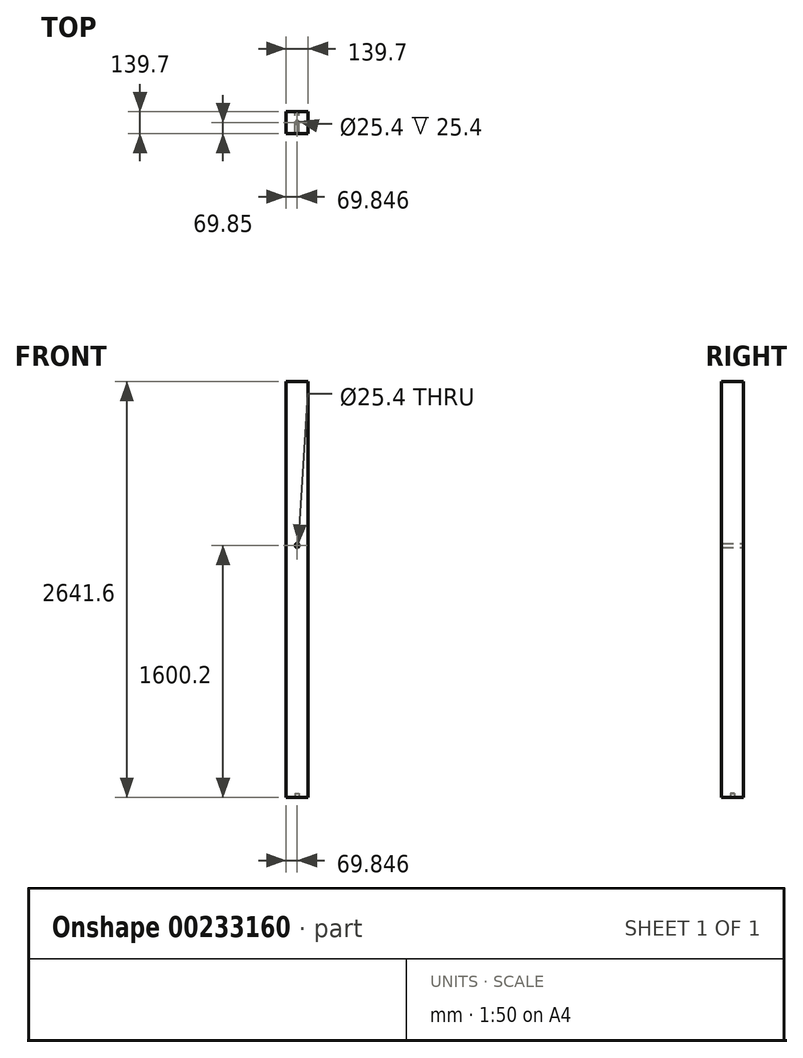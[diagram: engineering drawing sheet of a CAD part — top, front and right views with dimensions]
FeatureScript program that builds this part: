
annotation { "Feature Type Name" : "Feature", "Feature Type Description" : "" }
export const myFeature = defineFeature(function(context is Context, id is Id, definition is map)
    precondition{}
    {
        {
            var Q0;
            Q0=qCreatedBy(makeId("Front.planeOp"),FACE);
            var sketch = newSketch(context, id + "F0", { "sketchPlane" : qUnion([Q0])});
            skLineSegment(sketch, "E0.bottom", {"start": v(-168.05, 2571.7) * mm, "end": v(-28.35, 2571.7) * mm});
            skLineSegment(sketch, "E0.top", {"start": v(-168.05, -69.9) * mm, "end": v(-28.35, -69.9) * mm});
            skLineSegment(sketch, "E0.left", {"start": v(-168.05, 2571.7) * mm, "end": v(-168.05, -69.9) * mm});
            skLineSegment(sketch, "E0.right", {"start": v(-28.35, 2571.7) * mm, "end": v(-28.35, -69.9) * mm});
            skCircle(sketch, "E1", {"center": v(-98.2, 1530.3) * mm, "radius": 12.7 * mm});
            skSolve(sketch);
        }
        {
            var Q0;
            Q0=makeQuery(id+"F0.imprint","IMPRINT",FACE,{"disambiguationData":[TD([[makeQuery(id+"F0.imprint","IMPRINT",EDGE,{"derivedFrom":sQuery(id+"F0.wireOp",EDGE,"E0.bottom")}),-1.0]])]});
            extrude(context, id + "F1", {"entities" : qUnion([Q0]), "depth" : 139.7 * mm});
        }
        {
            var Q0;
            Q0=makeQuery(id+"F1.opExtrude","SWEPT_FACE",FACE,{"disambiguationData":[OSD([sQuery(id+"F0.wireOp",EDGE,"E0.top")])]});
            var sketch = newSketch(context, id + "F2", { "sketchPlane" : qUnion([Q0])});
            skCircle(sketch, "E2", {"center": v(-98.2, 69.85) * mm, "radius": 12.7 * mm});
            skSolve(sketch);
        }
        {
            var Q0;
            Q0 = qSketchRegion(id + "F2", true);
            extrude(context, id + "F3", {"entities" : qUnion([Q0]), "operationType" : NewBodyOperationType.REMOVE, "oppositeDirection" : true, "depth" : 25.4 * mm});
        }
    });
